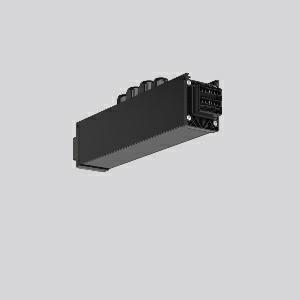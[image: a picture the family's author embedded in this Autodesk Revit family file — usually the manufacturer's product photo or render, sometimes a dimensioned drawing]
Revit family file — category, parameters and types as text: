
# Revit family: linedo_mitteleinspeisung_14pol_s_s_982698_003_2_e364
name_source: partatom
category: Lighting Fixtures
units: mm (PartAtom-declared; Revit-internal decimal feet)

## family parameters
Cut with Voids When Loaded = No
Host = Face
Light Source = No
Part Type = Normal
Room Calculation Point = No
Round Connector Dimension = Use Diameter
Shared = No

## types (1)
- LINEDO_Mitteleinspeisung_14pol_S_S
    Apparent Load = 0 VA
    Default Elevation = 1800 mm
    Description = Series: LINEDO
Middle power feed, 14-pole, connection plug / plug. Housing: extruded aluminium profile, powder-coated. Cover made of plastic, surface like housing. LINEDO plug system, plastic, black. 4 cable glands (2 x M20 and 2 x M25). Cable glands on top. Easy connection for rigid or flexible wires.
Colour: black
Length: 349 mm
Width: 58 mm
Height: 76 mm
Weight: 850 g
    Height = 76 mm
    Lamp = 0 x
    Length = 349 mm
    Luminous efficacy = 0 lm/W
    Manufacturer = RZB
    ModVariant = No
    Model = 982698.003.2
    Mounting Place = Ceiling
    Mounting Type = Surface mounted, Pendant
    Number of Poles = 1
    OnlyDefault = Yes
    Power Factor = 1
    Product Name = LINEDO_Mitteleinspeisung_14pol_S_S
    Product group = Continuous line luminaire system Linedo IP 54
    ProductGroupID = 314
    Protection Class = Protection class I
    Protection Degree = IP 54
    RLX_Detail_Level = 1
    RLX_Emergency_Light_Flux = 0 lm
    RLX_Emergency_Type = 0
    RLX_Emergency_Type_DB = No
    RlxData = <blob elided: 23377 chars, md5=74361c0d>
    Standby Power = 0 W
    System Light Flux = 0 lm
    System Power = 0 W
    Type Comments = Product without accessories
    Type Image = 982698.003.2.jpg
    URL = http://relux.com
    VarID = ---
    Voltage = 0 V
    Weight = 0.00 kg
    Width = 58 mm

## geometry (parser evidence)
native form markers: Blend x4, Sweep x11
no freeform markers — native parametric forms only
